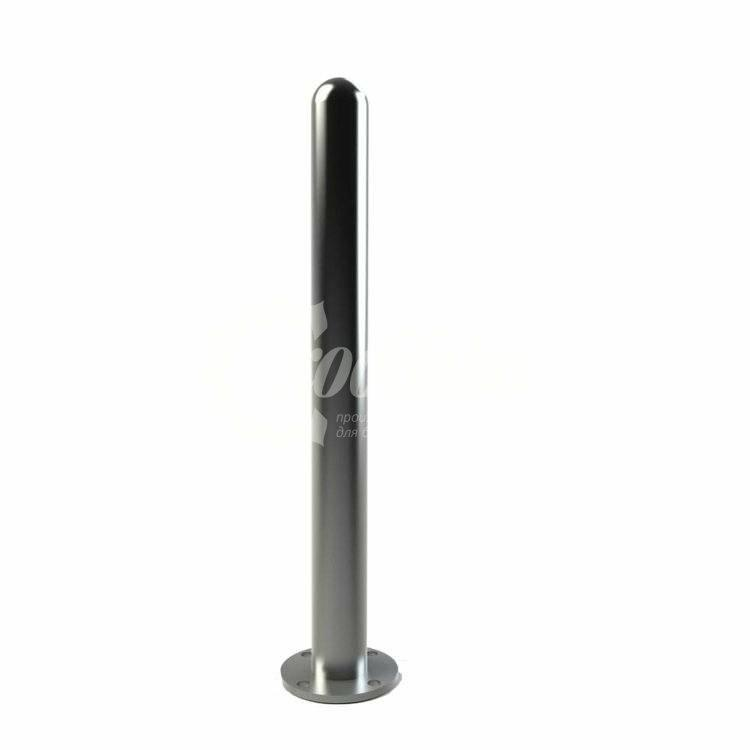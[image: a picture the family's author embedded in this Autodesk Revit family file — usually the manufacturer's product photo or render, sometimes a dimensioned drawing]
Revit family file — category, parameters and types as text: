
# Revit family: 10211 Столбик парковочный нержавеющий «Сфера» Хоббика
name_source: partatom
category: Антураж
revit_build: Autodesk Revit 2018 (Build: 20180423_1000(x64)
units: mm (PartAtom-declared; Revit-internal decimal feet)

## family parameters
Всегда вертикально = Да
Источник визуального образа = Геометрия семейства
На основе рабочей плоскости = Нет
Общий = Нет
При загрузке вырезать с полостями = Нет
Точка расчета площади = Нет

## types (2) — shared parameters
URL = https://hobbyka.ru
Артикул товара = Арт. 10211
Группа модели = Тротуарные столбики и ограждения
Диаметр = 76 мм
Длина = 76 мм
Изготовитель = ООО «Хоббика»
Изображение типоразмера = Столбик парковочный нержавеющий «Сфера» Арт 10211.jpg
Материал изделия = Сталь
Цвет каркаса = Сталь
Ширина = 76 мм

## per-type parameters (varying)
| type | Версия 0,785 м | Версия 1,2 м | Высота | Описание |
| Версия 0,785 м | Да | Нет | 785 мм | Столбик парковочный нержавеющий «Сфера». Версия 0,785 м |
| Версия 1,2 м | Нет | Да | 1200 мм | Столбик парковочный нержавеющий «Сфера». Версия 1,2 м |
